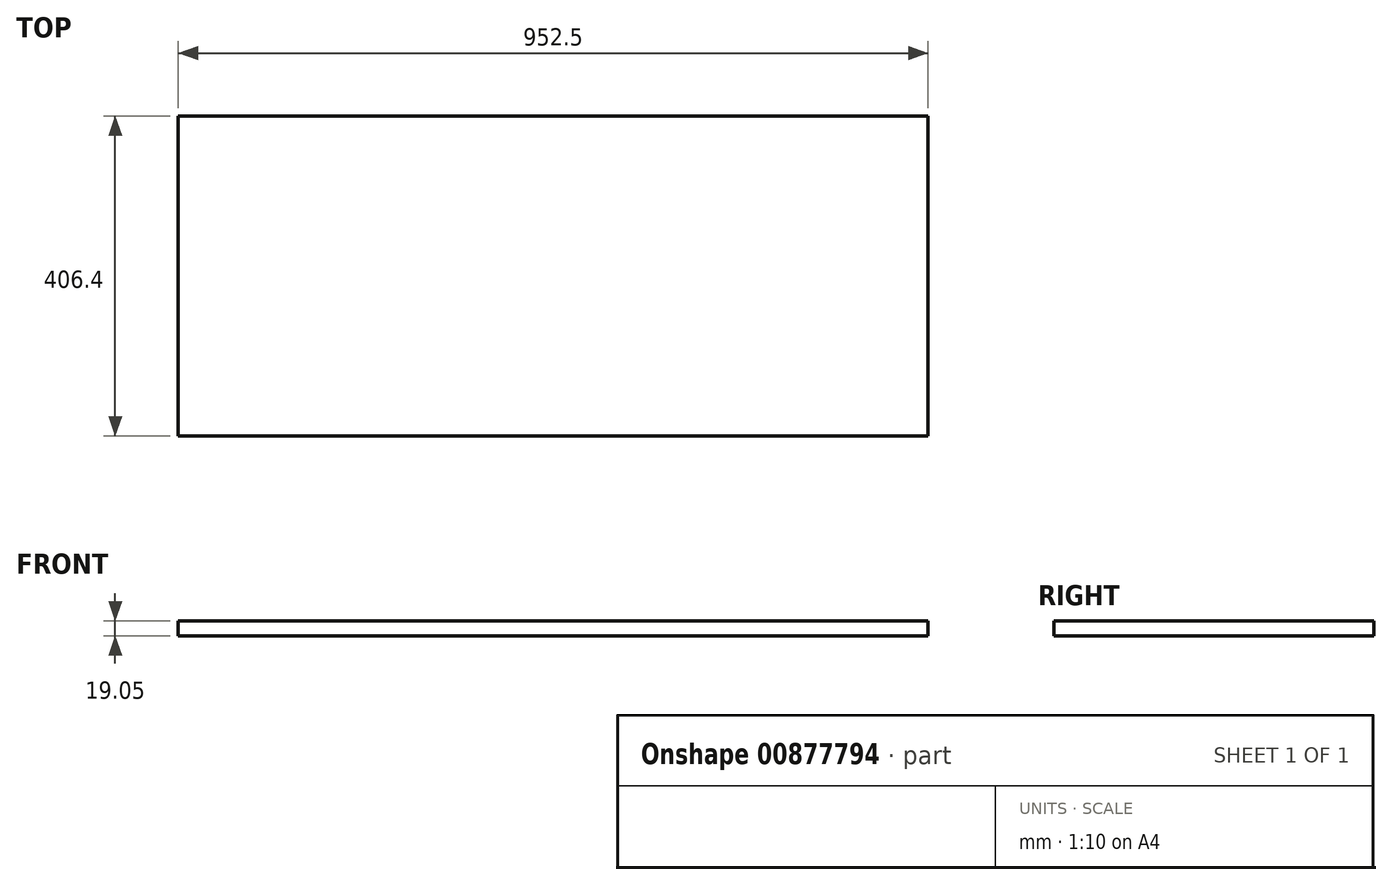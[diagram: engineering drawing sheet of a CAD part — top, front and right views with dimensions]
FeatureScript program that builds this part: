
annotation { "Feature Type Name" : "Feature", "Feature Type Description" : "" }
export const myFeature = defineFeature(function(context is Context, id is Id, definition is map)
    precondition{}
    {
        {
            var Q0;
            Q0=qCreatedBy(makeId("Top.planeOp"),FACE);
            var sketch = newSketch(context, id + "F0", { "sketchPlane" : qUnion([Q0])});
            skLineSegment(sketch, "E0.bottom", {"start": v(-482.79, 135.66) * mm, "end": v(469.71, 135.66) * mm});
            skLineSegment(sketch, "E0.top", {"start": v(-482.79, -270.74) * mm, "end": v(469.71, -270.74) * mm});
            skLineSegment(sketch, "E0.left", {"start": v(-482.79, 135.66) * mm, "end": v(-482.79, -270.74) * mm});
            skLineSegment(sketch, "E0.right", {"start": v(469.71, 135.66) * mm, "end": v(469.71, -270.74) * mm});
            skSolve(sketch);
        }
        {
            var Q0;
            Q0=makeQuery(id+"F0.imprint","IMPRINT",FACE,{"disambiguationData":[TD([[makeQuery(id+"F0.imprint","IMPRINT",EDGE,{"derivedFrom":sQuery(id+"F0.wireOp",EDGE,"E0.bottom")}),-1.0]])]});
            extrude(context, id + "F1", {"entities" : qUnion([Q0]), "depth" : 19.05 * mm, "offsetDistance" : 25.4 * mm});
        }
    });
